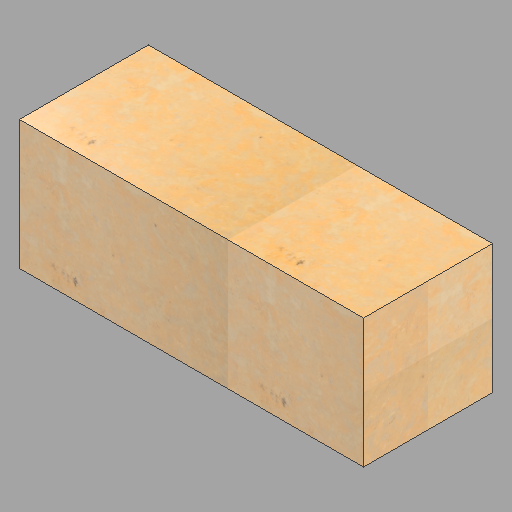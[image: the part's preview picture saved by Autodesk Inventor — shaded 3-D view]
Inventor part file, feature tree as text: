
AUTODESK INVENTOR PART (.ipt)
format: ipt  version: 2022.2 (Build 262287010, 287A)  size: 327,168 bytes
history: native  units: in
note: dims shown in document units (in); Inventor stores cm internally (conversion verified against a paired STEP export)
features: other x1, extrude x1, sketch x1
ambient origin geometry x8: Origin, YZ Plane, XZ Plane, XY Plane, X Axis, Y Axis, Z Axis, Center Point
bodies: Solid1 (feature_tree)
feature tree (3):
  other  "Bench - 34"
  extrude  "Extrusion1"  Depth=18.0in
  sketch  "Sketch1"  dims[d0=18.0in d1=18.0in d2=48.0in d3=0.0in]
